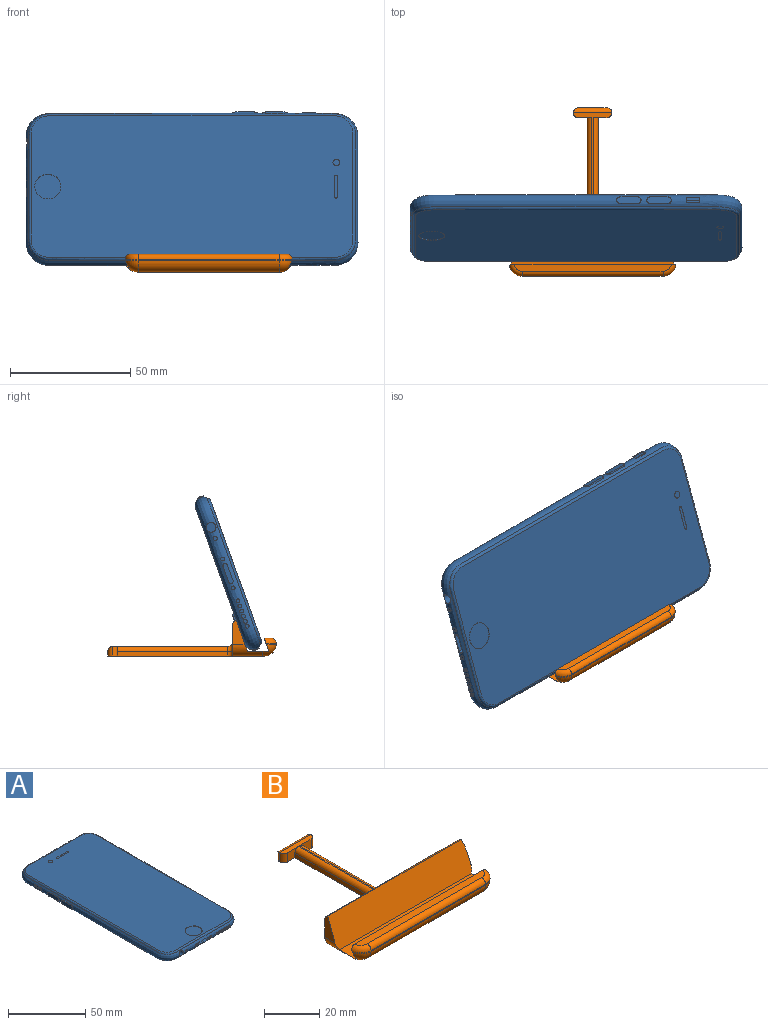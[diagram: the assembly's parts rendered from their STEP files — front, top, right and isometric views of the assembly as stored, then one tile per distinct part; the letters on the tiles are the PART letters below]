
ASSEMBLY  parts=2 mates=1
PART A: 76 faces, bbox 67.9x138.3x7.9 mm
  f0: cylinder r=0.8mm len=1.6mm, axis (0,1,0), area 1mm2, adj f18,f75
  f1: cylinder r=0.8mm len=1.6mm, axis (0,1,0), area 1mm2, adj f18,f74
  f2: cylinder r=0.8mm len=1.6mm, axis (0,-1,0), area 0.9mm2, adj f18,f73
  f3: cylinder r=0.8mm len=1.6mm, axis (0,-1,0), area 1mm2, adj f18,f72
  f4: cylinder r=0.8mm len=1.6mm, axis (0,-1,0), area 1mm2, adj f18,f71
  f5: cylinder r=0.8mm len=1.6mm, axis (0,-1,0), area 1mm2, adj f18,f70
  f6: cylinder r=0.8mm len=1.6mm, axis (0,-1,0), area 1mm2, adj f18,f69
  f7: cylinder r=0.8mm len=1.6mm, axis (0,-1,0), area 1mm2, adj f18,f68
  f8: cylinder r=0.8mm len=1.6mm, axis (0,-1,0), area 1mm2, adj f18,f67
  f9: cylinder r=2.02mm len=14.4mm, axis (0,1,0), area 182mm2, adj f18,f66
  f10: cylinder r=0.56mm len=1.11mm, axis (-1,0,0), area 0.7mm2, adj f18,f60
  f11: cylinder r=5.45mm len=10.9mm, axis (0,0,1), area 8.6mm2, adj f20,f30
  f12: cylinder r=1.43mm len=2.85mm, axis (0,0,1), area 0.1mm2, adj f20,f29
  f13: cylinder r=0.6mm len=1.2mm, axis (0,0,1), area 0.2mm2, adj f20,f26,f27,f28
  f14: cylinder r=2.06mm len=4.11mm, axis (0,0,-1), area 1.3mm2, adj f21,f24
  f15: cylinder r=0.75mm len=1.5mm, axis (0,0,-1), area 0.5mm2, adj f21,f23
  f16: cylinder r=3.6mm len=7.2mm, axis (0,0,1), area 17.4mm2, adj f21,f22
  f17: bspline ~135.99x64.82mm, area 589.2mm2, adj f18,f20
  f18: bspline ~138.14x66.97mm, area 2894.6mm2, adj f0,f1,f2,f3,f4,f5,f6,f7
  f19: plane 1.02x0.41mm, normal (0,1,0), area 0.3mm2, adj f18,f31,f35,f36
  f20: plane 134.1x62.93mm, normal (0,0,1), area 8237.3mm2, adj f11,f12,f13,f17,f25,f26,f27
  f21: plane 132x60.83mm, normal (0,0,-1), area 7934.9mm2, adj f14,f15,f16,f18
  f22: plane 7.2x7.2mm, normal (0,0,-1), area 40.7mm2, adj f16
  f23: plane 1.5x1.5mm, normal (0,0,-1), area 1.8mm2, adj f15
  f24: plane 4.11x4.11mm, normal (0,0,-1), area 13.3mm2, adj f14
  f25: cylinder r=0.6mm len=1.2mm, axis (0,0,1), area 0.2mm2, adj f20,f26,f27,f28
  f26: plane 9x0.1mm, normal (0,-1,0), area 0.9mm2, adj f13,f20,f25,f28
  f27: plane 9x0.1mm, normal (0,1,0), area 0.9mm2, adj f13,f20,f25,f28
  f28: plane 10.2x1.2mm, normal (0,0,1), area 11.9mm2, adj f13,f25,f26,f27
  f29: plane 2.85x2.85mm, normal (0,0,1), area 6.4mm2, adj f12
  f30: plane 10.9x10.9mm, normal (0,0,1), area 93.3mm2, adj f11
  f31: cylinder r=0.25mm len=0.28mm, axis (1,0,0), area 0.1mm2, adj f18,f19,f32,f35
  f32: plane 5.12x0.21mm, normal (0,0,-1), area 1mm2, adj f18,f31,f33,f35
  f33: cylinder r=0.25mm len=0.27mm, axis (1,0,0), area 0.1mm2, adj f18,f32,f34,f35
  f34: plane 1.01x0.41mm, normal (0,-1,0), area 0.3mm2, adj f18,f33,f35,f38
  f35: plane 5.61x1.24mm, normal (-1,0,0), area 5.6mm2, adj f19,f31,f32,f33,f34,f36,f37,f38
  f36: cylinder r=0.25mm len=0.81mm, axis (1,0,0), area 0.3mm2, adj f19,f35,f37,f43,f44
  f37: plane 5.11x0.81mm, normal (0,0,1), area 4.1mm2, adj f35,f36,f38,f44
  f38: cylinder r=0.25mm len=0.81mm, axis (1,0,0), area 0.3mm2, adj f34,f35,f37,f39,f44
  f39: plane 0.51x0.49mm, normal (0,1,0), area 0.2mm2, adj f18,f38,f40,f44
  f40: cylinder r=0.25mm len=0.57mm, axis (1,0,0), area 0.2mm2, adj f18,f39,f41,f44
  f41: plane 5.12x0.58mm, normal (0,0,-1), area 2.9mm2, adj f18,f40,f42,f44
  f42: cylinder r=0.25mm len=0.57mm, axis (1,0,0), area 0.2mm2, adj f18,f41,f43,f44
  f43: plane 0.51x0.5mm, normal (0,-1,0), area 0.2mm2, adj f18,f36,f42,f44
  f44: plane 5.61x0.99mm, normal (-1,0,0), area 5.5mm2, adj f36,f37,f38,f39,f40,f41,f42,f43
  f45: plane 7.41x0.64mm, normal (0,0,1), area 4.6mm2, adj f18,f46,f48,f49
  f46: cylinder r=1.4mm len=2.8mm, axis (1,0,0), area 2mm2, adj f18,f45,f47,f49
  f47: plane 7.4x0.6mm, normal (0,0,-1), area 4.4mm2, adj f18,f46,f48,f49
  f48: cylinder r=1.4mm len=2.8mm, axis (1,0,0), area 2mm2, adj f18,f45,f47,f49
  f49: plane 10.2x2.8mm, normal (-1,0,0), area 26.9mm2, adj f45,f46,f47,f48
  f50: plane 7.4x0.62mm, normal (0,0,1), area 4.5mm2, adj f18,f51,f53,f54
  f51: cylinder r=1.4mm len=2.8mm, axis (1,0,0), area 2mm2, adj f18,f50,f52,f54
  f52: plane 7.4x0.59mm, normal (0,0,-1), area 4.4mm2, adj f18,f51,f53,f54
  f53: cylinder r=1.4mm len=2.8mm, axis (1,0,0), area 2mm2, adj f18,f50,f52,f54
  f54: plane 10.2x2.8mm, normal (-1,0,0), area 26.9mm2, adj f50,f51,f52,f53
  f55: cylinder r=1.4mm len=2.8mm, axis (-1,0,0), area 2mm2, adj f18,f56,f58,f59
  f56: plane 7.41x0.64mm, normal (0,0,1), area 4.6mm2, adj f18,f55,f57,f59
  f57: cylinder r=1.4mm len=2.8mm, axis (-1,0,0), area 2mm2, adj f18,f56,f58,f59
  f58: plane 7.4x0.6mm, normal (0,0,-1), area 4.4mm2, adj f18,f55,f57,f59
  f59: plane 10.2x2.8mm, normal (1,0,0), area 26.9mm2, adj f55,f56,f57,f58
  f60: plane 1.11x1.11mm, normal (1,0,0), area 1mm2, adj f10
  f61: cylinder r=0.99mm len=6.47mm, axis (0,1,0), area 20.1mm2, adj f18,f62,f64,f65
  f62: plane 6.72x6.44mm, normal (0,0,1), area 43.3mm2, adj f18,f61,f63,f65
  f63: cylinder r=0.99mm len=6.47mm, axis (0,1,0), area 20.1mm2, adj f18,f62,f64,f65
  f64: plane 6.73x6.48mm, normal (0,0,-1), area 43.5mm2, adj f18,f61,f63,f65
  f65: plane 8.7x1.98mm, normal (0,-1,0), area 16.4mm2, adj f61,f62,f63,f64
  f66: plane 4.04x4.04mm, normal (0,-1,0), area 12.8mm2, adj f9
  f67: plane 1.6x1.6mm, normal (0,-1,0), area 2mm2, adj f8
  f68: plane 1.6x1.6mm, normal (0,-1,0), area 2mm2, adj f7
  f69: plane 1.6x1.6mm, normal (0,-1,0), area 2mm2, adj f6
  f70: plane 1.6x1.6mm, normal (0,-1,0), area 2mm2, adj f5
  f71: plane 1.6x1.6mm, normal (0,-1,0), area 2mm2, adj f4
  f72: plane 1.6x1.6mm, normal (0,-1,0), area 2mm2, adj f3
  f73: plane 1.6x1.6mm, normal (0,-1,0), area 2mm2, adj f2
  f74: plane 1.6x1.6mm, normal (0,-1,0), area 2mm2, adj f1
  f75: plane 1.6x1.6mm, normal (0,-1,0), area 2mm2, adj f0
PART B: 41 faces, bbox 70.4x70.5x15.1 mm
  f0: plane 10x5.14mm, normal (-1,0,0), area 32.4mm2, adj f7,f11,f23,f40
  f1: plane 47.94x16mm, normal (0,0,1), area 55.7mm2, adj f9,f10,f13,f15,f25,f27,f28,f31
  f2: plane 12x2mm, normal (0,1,0), area 24mm2, adj f3,f33,f34,f35
  f3: plane 65x59.56mm, normal (0,0,-1), area 1058.3mm2, adj f2,f9,f10,f11,f12,f13,f14,f15
  f4: plane 58.56x0.4mm, normal (0,-1,0), area 23.1mm2, adj f16,f17,f21,f38
  f5: plane 69.28x5.4mm, normal (0,0.94,-0.34), area 392.4mm2, adj f6,f16,f17,f20,f22,f36,f37,f39
  f6: plane 67.56x8.83mm, normal (0,0,1), area 595.5mm2, adj f5,f7,f19,f20,f22,f23
  f7: plane 69.62x13.06mm, normal (0,-0.94,0.34), area 955.7mm2, adj f0,f6,f8,f18,f19,f23,f40
  f8: plane 0.38x0.14mm, normal (1,0,0), area 0mm2, adj f7,f18,f19
  f9: plane 4x0.05mm, normal (1,0,0), area 0.2mm2, adj f1,f3,f32,f33
  f10: plane 4x0.05mm, normal (-1,0,0), area 0.2mm2, adj f1,f3,f31,f34
  f11: plane 64.56x13.06mm, normal (0,1,0), area 793.7mm2, adj f0,f3,f18,f23,f24,f26,f27,f29
  f12: plane 45.89x2mm, normal (-1,0,0), area 91.8mm2, adj f3,f13,f24,f25
  f13: plane 5.72x4mm, normal (0,-1,0), area 15.8mm2, adj f1,f3,f12,f25,f31
  f14: plane 45.89x2mm, normal (1,0,0), area 91.8mm2, adj f3,f15,f28,f30
  f15: plane 5.74x4mm, normal (0,-1,0), area 15.8mm2, adj f1,f3,f14,f28,f32
  f16: cylinder r=5.5mm len=5.35mm, axis (0,0,1), area 2.9mm2, adj f4,f5,f22,f37
  f17: cylinder r=5.5mm len=5.35mm, axis (0,0,-1), area 2.9mm2, adj f4,f5,f20,f39
  f18: cylinder r=5mm len=15mm, axis (0,0,1), area 82.6mm2, adj f7,f8,f11,f19,f40
  f19: cylinder r=5mm len=12.56mm, axis (0,-1,0), area 62.3mm2, adj f3,f6,f7,f8,f18,f20
  f20: torus R=0.5mm, axis (0,0,1), area 38.9mm2, adj f3,f5,f6,f17,f19,f21
  f21: cylinder r=5mm len=58.56mm, axis (1,0,0), area 459.9mm2, adj f3,f4,f20,f22
  f22: torus R=0.5mm, axis (0,0,1), area 38.9mm2, adj f3,f5,f6,f16,f21,f23
  f23: cylinder r=5mm len=12.56mm, axis (0,1,0), area 76.5mm2, adj f0,f3,f6,f7,f11,f22
  f24: cylinder r=2mm len=2mm, axis (0,0,-1), area 6.3mm2, adj f3,f11,f12,f26
  f25: cylinder r=2mm len=45.89mm, axis (0,-1,0), area 144.2mm2, adj f1,f12,f13,f26
  f26: torus R=4mm, axis (0,-1,0), area 13.5mm2, adj f11,f24,f25,f27
  f27: cylinder r=2mm len=2mm, axis (-1,0,0), area 1.7mm2, adj f1,f11,f26,f29
  f28: cylinder r=2mm len=45.89mm, axis (0,1,0), area 144.2mm2, adj f1,f14,f15,f29
  f29: torus R=4mm, axis (0,-1,0), area 13.5mm2, adj f11,f27,f28,f30
  f30: cylinder r=2mm len=2mm, axis (0,0,1), area 6.3mm2, adj f3,f11,f14,f29
  f31: cylinder r=2mm len=4mm, axis (0,0,-1), area 12.6mm2, adj f1,f3,f10,f13
  f32: cylinder r=2mm len=4mm, axis (0,0,1), area 12.6mm2, adj f1,f3,f9,f15
  f33: cylinder r=2mm len=4mm, axis (0,0,1), area 10.3mm2, adj f2,f3,f9,f35
  f34: cylinder r=2mm len=4mm, axis (0,0,-1), area 10.3mm2, adj f2,f3,f10,f35
  f35: cylinder r=2mm len=16mm, axis (-1,0,0), area 45.7mm2, adj f1,f2,f33,f34
  f36: plane 65.48x2.96mm, normal (0,0,1), area 189.1mm2, adj f5,f37,f38,f39
  f37: torus R=3.5mm, axis (0,0,-1), area 21mm2, adj f5,f16,f36,f38
  f38: cylinder r=2mm len=58.56mm, axis (-1,0,0), area 184mm2, adj f4,f36,f37,f39
  f39: torus R=3.5mm, axis (0,0,-1), area 21mm2, adj f5,f17,f36,f38
  f40: cylinder r=2mm len=68.13mm, axis (-1,0,0), area 175.3mm2, adj f0,f7,f11,f18
PLACE A rot(axis=(0.5,0.5,-0.71),109.2deg) t=(-6.92,-6.84,34.39)mm
PLACE B at identity fixed
MATE planar B.f7 <-> A.f21  axis (0,-0.94,0.34) through (-0.16,-12.59,8.49)mm
